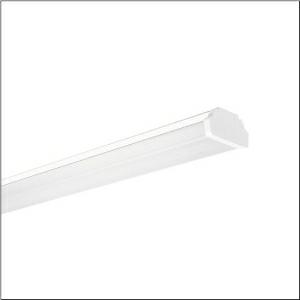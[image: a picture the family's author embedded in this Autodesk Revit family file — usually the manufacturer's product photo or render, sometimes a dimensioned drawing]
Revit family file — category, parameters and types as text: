
# Revit family: dus_r__31_gen_2_53bd812cv49xc2_1e0d
name_source: partatom
category: Lighting Fixtures
units: mm (PartAtom-declared; Revit-internal decimal feet)

## family parameters
Cut with Voids When Loaded = No
Host = Face
Light Source = No
Part Type = Normal
Room Calculation Point = No
Round Connector Dimension = Use Diameter
Shared = No

## types (1)
- --- (1 x LED, 9240 lm, 49.9 W, 4000K)
    Apparent Load = 50 VA
    CIE Flux Codes = 47 80 95 93 100
    Color Rendering = 80
    Color Temperature = 4000K
    Default Elevation = 1800 mm
    Description = DUS® 31 Gen.2, luminaire insert, of sheet steel, coil coated, white, length: 1.535mm, width: 81mm, height: 90mm, 5x system unit, system units: 307mm, LED rated luminous flux: 9.240lm, light colour: 840, control gear: ON/OFF Multilumen, CLOi, with plug, 3-pole, with phase selection, mains connection: 220..240V, AC, 50/60Hz, start of lifetime: 50W, end of service life: 61W, through-wiring accessed according to module size, primary optical cover: cover, of PMMA, light emission: direct distribution, primary light characteristic: symmetric, protection rating (complete): IP20, protection rating (LED compartment): IP50, insulation class (complete): insulation class I (protective earthing), certification: CE, ENEC, VDE, UKCA, impact resistance: IK03, permissible ambient temperature for indoor applications: -35..+40°C, corresponds to IFS (International Featured Standards) requirements for safety and quality in the food industry, reducing of maximum allowable ambient temperature of 5°C with ceiling mounting, packaging unit: 1 piece
    Height = 95 mm
    Lamp = 1 x LED
    Lamp Light Flux = 9240 lm
    Lamp Power = 49.9 W
    Lamp count = 1
    Length = 1535 mm
    Luminous efficacy = 185 lm/W
    Manufacturer = Siteco
    ModVariant = No
    Model = 53BD812CV49XC2
    Mounting Place = Ceiling
    Mounting Type = Pendant
    Number of Poles = 1
    OnlyDefault = Yes
    Power Factor = 1
    Product Name = DUS® 31 Gen.2
    Product group = luminaire insert
    ProductGroupID = 902
    Protection Class = Protection class I
    Protection Degree = IP 20
    RLX_Detail_Level = 1
    RLX_Emergency_Light_Flux = 0 lm
    RLX_Emergency_Type = 0
    RLX_Emergency_Type_DB = No
    RlxData = <blob elided: 29681 chars, md5=1904e19a>
    Socket = socket
    Standby Power = 0 W
    System Light Flux = 9240 lm
    System Power = 50 W
    Type Comments = factory setting: luminous flux: 100 % | (A | C | E) | 116 mA
    Type Image = l_1319596.jpg
    URL = http://relux.com
    VarID = @adj_042260
    Voltage = 0 V
    Weight = 0.00 kg
    Width = 81 mm

## geometry (parser evidence)
native form markers: Blend x4, Sweep x11
no freeform markers — native parametric forms only
